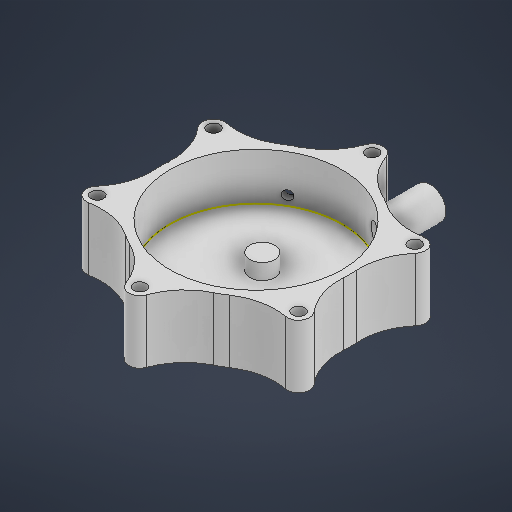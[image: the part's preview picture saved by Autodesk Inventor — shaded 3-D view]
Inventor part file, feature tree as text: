
AUTODESK INVENTOR PART (.ipt)
format: ipt  version: 2025.3 (Build 293356000, 356)  size: 324,096 bytes
history: native  units: mm
features: sketch x6, extrude x6, plane x2
ambient origin geometry x8: Origin, YZ Plane, XZ Plane, XY Plane, X Axis, Y Axis, Z Axis, Center Point
bodies: Body1 (feature_tree)
feature tree (14):
  sketch  "Sketch1"  dims[d16=60.0mm d17=55.0mm]
  extrude  "Extrusion5"  Depth=55.0mm
  extrude  "Extrusion6"  Depth=37.0mm
  sketch  "Sketch4"  dims[d21=20.0mm d22=4.0mm]
  plane  "Work Plane3"
  sketch  "Sketch5"  dims[d23=60.0mm d25=360.0deg d27=20.0mm d28=0.0mm]
  extrude  "Extrusion7"  Depth=4.0mm
  extrude  "Extrusion8"  Depth=20.0mm TaperAngle=0.0deg
  plane  "Work Plane4"
  extrude  "Extrusion9"  Depth=10.0mm
  extrude  "Extrusion11"  Depth=5.0mm
  sketch  "Sketch Circular Pattern1"  dims[d18=7.0mm d19=37.0mm]
  sketch  "Sketch6"  dims[d29=5.0mm d30=0.0mm d33=10.0mm]
  sketch  "Sketch8"  dims[d34=6.0mm d35=8.0mm d36=15.0mm d37=3.0mm d38=0.0mm d39=10.0mm d40=0.0mm d41=3.0mm d42=3.0mm d43=8.0mm d44=10.0mm d45=0.0mm d53=5.0mm d54=0.0mm d57=8.0mm d58=45.0mm d59=2.0mm d3=0.5mm d4=0.872665mm d5=0.5mm d6=0.872665mm d60=0.5mm d61=0.872665mm d62=0.5mm d63=0.872665mm]
